# Revit family: Legrand_Gestion_eclairage_Actionneur_KNX
name_source: partatom
category: Dispositifs d'éclairage
units: mm (PartAtom-declared; Revit-internal decimal feet)

## family parameters
Conserver l'orientation des annotations = Non
Cote de connecteur circulaire = Utiliser le diamètre
Couper avec des vides une fois chargée = Non
Hôte = Face
Partagée = Non
Point de calcul de pièce = Non
Type d'élément = Normal

## types (2) — shared parameters
Adapté pour transmission sans fil = Non
Classe de protection (IP) = IP20
Collecteur de terre = Non
Condition Générale d'Utilisation = https://export.legrand.com
Cosses d'artère secondaire = Non
Couleur = <Par catégorie>
Coupure forcée = Non
Elévation par défaut = 1219 mm
Entrée secondaire = Non
Fabricant = Legrand
Fonction variateur intégré = Non
Gestion CVC = Non
Gestion alarme = Non
Liaison neutre = Non
Mode de montage = autre
Réglage de lumière constante = Non
Sensibilité lumineuse réglable = Non
Sensibilité réglable = Non
Télécommandable = Non
URL = http://www.legrandoc.com
zero-valued in all types: Angle de détection horizontal (MAX) (°), Angle de détection horizontal (MIN) (°), Capacité de coupure max. (W), Courant de démarrage max. (A), Diamètre de détection sur le plancher (m), Durée d'enclenchement max. (mn), Durée d'enclenchement min. (s), Fréquence (MAX) (Hz), Fréquence (MIN) (Hz), Hauteur de montage maximale (m), Numéro RAL, Portée max. frontale (m), Portée max. latérale (m), Sensibilité lumineuse (MAX) (lx), Sensibilité lumineuse (MIN) (lx), Température (MAX) (°C), Température (MIN) (°C), Tension nominale (V)

## per-type parameters (varying)
| type | DALI 4 sorties | Description | Modèle | Variation 10-10V 4 sorties |
| Variation 1-10V 4 sorties | Non | KNX CONTROLLEUR FAUX PLAFOND 4 SORTIES 1-10V | 048887 | Oui |
| DALI 4 sorties | Oui | KNX CONTROLLEUR FAUX PLAFOND 4 SORTIES DALI | 048888 | Non |
